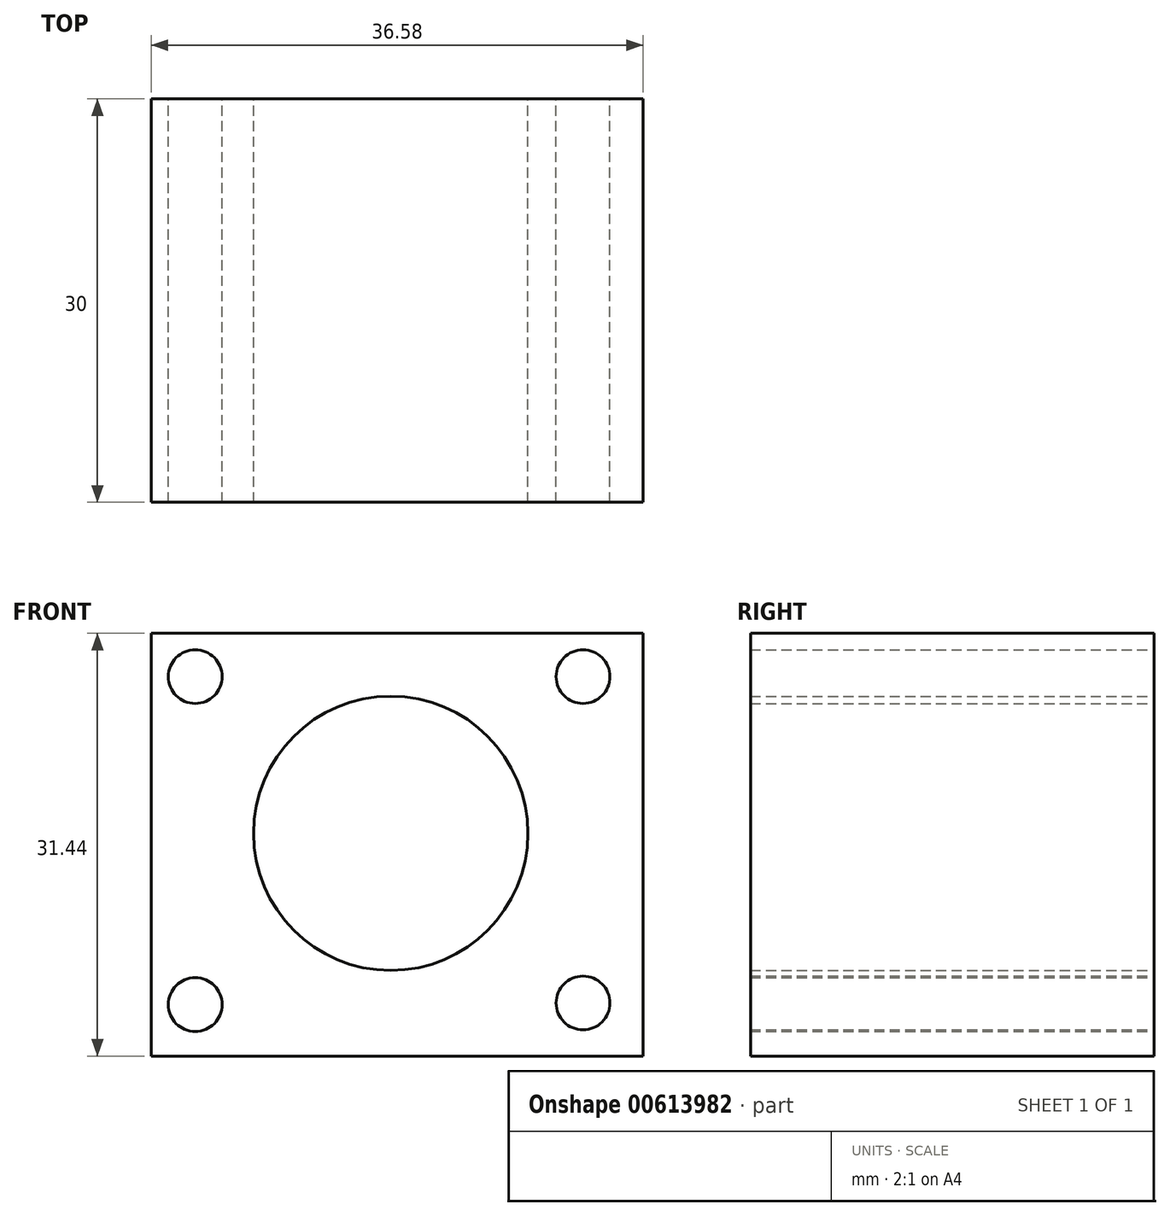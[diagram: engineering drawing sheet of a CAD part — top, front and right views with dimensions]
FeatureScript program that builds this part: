
annotation { "Feature Type Name" : "Feature", "Feature Type Description" : "" }
export const myFeature = defineFeature(function(context is Context, id is Id, definition is map)
    precondition{}
    {
        {
            var Q0;
            Q0=qCreatedBy(makeId("Front.planeOp"),FACE);
            var sketch = newSketch(context, id + "F0", { "sketchPlane" : qUnion([Q0])});
            skLineSegment(sketch, "E0.bottom", {"start": v(-52.2, 36.27) * mm, "end": v(-15.62, 36.27) * mm});
            skLineSegment(sketch, "E0.top", {"start": v(-52.2, 4.83) * mm, "end": v(-15.62, 4.83) * mm});
            skLineSegment(sketch, "E0.left", {"start": v(-52.2, 36.27) * mm, "end": v(-52.2, 4.83) * mm});
            skLineSegment(sketch, "E0.right", {"start": v(-15.62, 36.27) * mm, "end": v(-15.62, 4.83) * mm});
            skCircle(sketch, "E1", {"center": v(-34.38, 21.4) * mm, "radius": 10.2 * mm});
            skCircle(sketch, "E2", {"center": v(-34.38, 21.4) * mm, "radius": 4.98 * mm});
            skCircle(sketch, "E3", {"center": v(-48.92, 33.05) * mm, "radius": 2 * mm});
            skCircle(sketch, "E4", {"center": v(-20.08, 33.05) * mm, "radius": 2 * mm});
            skCircle(sketch, "E5", {"center": v(-20.08, 8.78) * mm, "radius": 2 * mm});
            skCircle(sketch, "E6", {"center": v(-48.92, 8.66) * mm, "radius": 2 * mm});
            skSolve(sketch);
        }
        {
            var Q0;
            Q0 = qSketchRegion(id + "F0", true);
            extrude(context, id + "F1", {"entities" : qUnion([Q0]), "depth" : 30 * mm, "offsetDistance" : 25 * mm});
        }
    });
